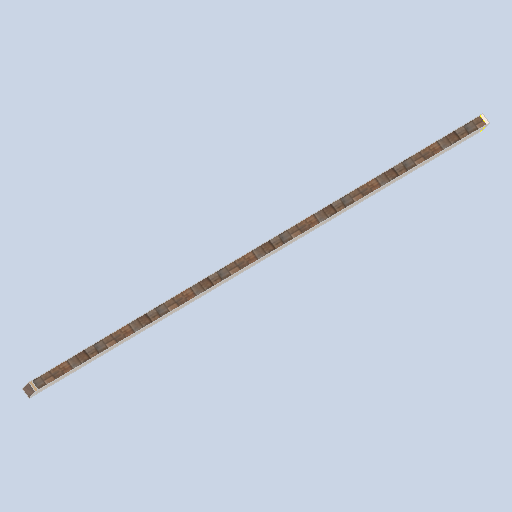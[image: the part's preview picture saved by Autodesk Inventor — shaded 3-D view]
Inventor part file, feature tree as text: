
AUTODESK INVENTOR PART (.ipt)
format: ipt  version: 2024.2 (Build 282272000, 272)  size: 135,680 bytes
history: native  units: in
note: dims shown in document units (in); Inventor stores cm internally (conversion verified against a paired STEP export)
features: sketch x5, other x3, plane x2
ambient origin geometry x8: Origin, YZ Plane, XZ Plane, XY Plane, X Axis, Y Axis, Z Axis, Center Point
bodies: Solid1 (feature_tree)
feature tree (10):
  other  "support_beam_segment_0106.ipt"
  other  "Solid1::support_beam_segment_0106.ipt"
  other  "TaggingFeature1"
  sketch  "Sketch1"  dims[d0=0.3937in]
  sketch  "Sketch2"
  sketch  "Sketch3"
  sketch  "Sketch4"
  sketch  "Sketch5"
  plane  "Work Plane1"
  plane  "Work Plane2"
